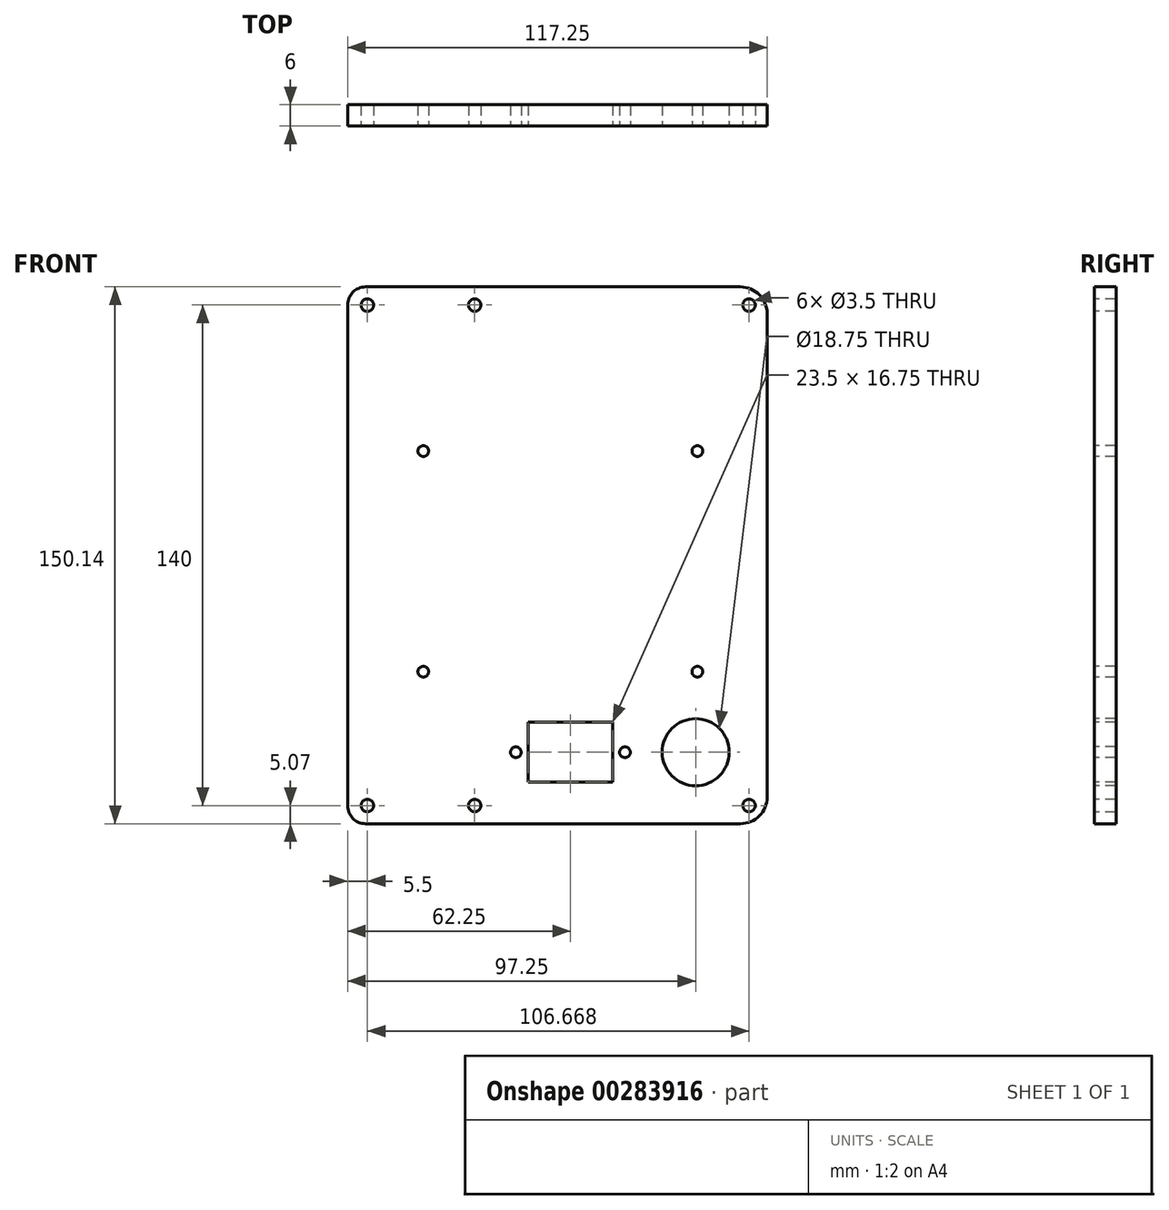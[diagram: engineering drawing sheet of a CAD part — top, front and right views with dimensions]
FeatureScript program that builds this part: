
annotation { "Feature Type Name" : "Feature", "Feature Type Description" : "" }
export const myFeature = defineFeature(function(context is Context, id is Id, definition is map)
    precondition{}
    {
        {
            var Q0;
            Q0=qCreatedBy(makeId("Front.planeOp"),FACE);
            var sketch = newSketch(context, id + "F0", { "sketchPlane" : qUnion([Q0])});
            skLineSegment(sketch, "E0.bottom", {"start": v(20.5, 75.07) * mm, "end": v(-20.5, 75.07) * mm});
            skLineSegment(sketch, "E0.top", {"start": v(20.5, -75.07) * mm, "end": v(-20.5, -75.07) * mm});
            skLineSegment(sketch, "E0.left", {"start": v(20.5, 75.07) * mm, "end": v(20.5, -75.07) * mm});
            skLineSegment(sketch, "E0.right", {"start": v(-20.5, 75.07) * mm, "end": v(-20.5, -75.07) * mm});
            skPoint(sketch, "E0.middle", {"position": v(0, 0) * mm});
            skSolve(sketch);
        }
        {
            var Q0;
            Q0 = qSketchRegion(id + "F0", true);
            extrude(context, id + "F1", {"entities" : qUnion([Q0]), "depth" : 6 * mm});
        }
        {
            var Q0;
            Q0=makeQuery(id+"F1.opExtrude","CAP_FACE",FACE,{"disambiguationData":[OSD([sQuery(id+"F0.wireOp",EDGE,"E0.bottom"),sQuery(id+"F0.wireOp",EDGE,"E0.top"),sQuery(id+"F0.wireOp",EDGE,"E0.left"),sQuery(id+"F0.wireOp",EDGE,"E0.right")])],"isStart":false});
            var sketch = newSketch(context, id + "F2", { "sketchPlane" : qUnion([Q0])});
            skLineSegment(sketch, "E1", {"start": v(0, 75.07) * mm, "end": v(0, 0) * mm, "construction": true});
            skLineSegment(sketch, "E2", {"start": v(0, 0) * mm, "end": v(-20.5, 0) * mm, "construction": true});
            skCircle(sketch, "E3", {"center": v(-15, 70) * mm, "radius": 1.75 * mm});
            skCircle(sketch, "E4.MirrorC", {"center": v(15, 70) * mm, "radius": 1.75 * mm});
            skCircle(sketch, "E5.MirrorC", {"center": v(-15, -70) * mm, "radius": 1.75 * mm});
            skCircle(sketch, "E6.MirrorC", {"center": v(15, -70) * mm, "radius": 1.75 * mm});
            skSolve(sketch);
        }
        {
            var Q0;
            Q0 = qSketchRegion(id + "F2", true);
            extrude(context, id + "F3", {"entities" : qUnion([Q0]), "operationType" : NewBodyOperationType.REMOVE, "endBound" : BoundingType.THROUGH_ALL, "oppositeDirection" : true, "depth" : 25 * mm});
        }
        {
            var Q0;
            Q0=makeQuery(id+"F1.opExtrude","CAP_FACE",FACE,{"disambiguationData":[OSD([sQuery(id+"F0.wireOp",EDGE,"E0.bottom"),sQuery(id+"F0.wireOp",EDGE,"E0.top"),sQuery(id+"F0.wireOp",EDGE,"E0.left"),sQuery(id+"F0.wireOp",EDGE,"E0.right")])],"isStart":false});
            var sketch = newSketch(context, id + "F4", { "sketchPlane" : qUnion([Q0])});
            skLineSegment(sketch, "E7.bottom", {"start": v(20.5, 75.07) * mm, "end": v(96.75, 75.07) * mm});
            skLineSegment(sketch, "E7.top", {"start": v(20.5, -75.07) * mm, "end": v(96.75, -75.07) * mm});
            skLineSegment(sketch, "E7.left", {"start": v(20.5, 75.07) * mm, "end": v(20.5, -75.07) * mm});
            skLineSegment(sketch, "E7.right", {"start": v(96.75, 75.07) * mm, "end": v(96.75, -75.07) * mm});
            skSolve(sketch);
        }
        {
            var Q0;
            Q0 = qSketchRegion(id + "F4", true);
            var Q1;
            Q1=makeQuery(id+"F1.opExtrude","CAP_FACE",FACE,{"disambiguationData":[OSD([sQuery(id+"F0.wireOp",EDGE,"E0.bottom"),sQuery(id+"F0.wireOp",EDGE,"E0.top"),sQuery(id+"F0.wireOp",EDGE,"E0.left"),sQuery(id+"F0.wireOp",EDGE,"E0.right")])],"isStart":true});
            extrude(context, id + "F5", {"entities" : qUnion([Q0]), "operationType" : NewBodyOperationType.ADD, "endBound" : BoundingType.UP_TO_SURFACE, "oppositeDirection" : true, "endBoundEntityFace" : qUnion([Q1]), "depth" : 25 * mm});
        }
        {
            var Q0;
            Q0=makeQuery(id+"F1.opExtrude","SWEPT_EDGE",EDGE,{"disambiguationData":[OSD([sQuery(id+"F0.wireOp",EDGE,"E0.bottom"),sQuery(id+"F0.wireOp",EDGE,"E0.right")])]});
            var Q1;
            Q1=makeQuery(id+"F1.opExtrude","SWEPT_EDGE",EDGE,{"disambiguationData":[OSD([sQuery(id+"F0.wireOp",EDGE,"E0.top"),sQuery(id+"F0.wireOp",EDGE,"E0.right")])]});
            fillet(context, id + "F6", {"entities" : qUnion([Q0, Q1]), "radius" : 5 * mm, "tangentPropagation" : true, "allowEdgeOverflow" : false});
        }
        {
            var Q0;
            Q0=makeQuery(id+"F5.opExtrude","SWEPT_EDGE",EDGE,{"disambiguationData":[OSD([sQuery(id+"F4.wireOp",EDGE,"E7.bottom"),sQuery(id+"F4.wireOp",EDGE,"E7.right")])]});
            var Q1;
            Q1=makeQuery(id+"F5.opExtrude","SWEPT_EDGE",EDGE,{"disambiguationData":[OSD([sQuery(id+"F4.wireOp",EDGE,"E7.top"),sQuery(id+"F4.wireOp",EDGE,"E7.right")])]});
            fillet(context, id + "F7", {"entities" : qUnion([Q0, Q1]), "radius" : 7.5 * mm, "tangentPropagation" : true, "allowEdgeOverflow" : false});
        }
        {
            var Q0;
            Q0=makeQuery(id+"F5.boolean.opBoolean","MERGE",FACE,{"derivedFrom":[makeQuery(id+"F1.opExtrude","CAP_FACE",FACE,{"disambiguationData":[OSD([sQuery(id+"F0.wireOp",EDGE,"E0.bottom"),sQuery(id+"F0.wireOp",EDGE,"E0.top"),sQuery(id+"F0.wireOp",EDGE,"E0.left"),sQuery(id+"F0.wireOp",EDGE,"E0.right")])],"isStart":false}),makeQuery(id+"F5.opExtrude","CAP_FACE",FACE,{"disambiguationData":[OSD([sQuery(id+"F4.wireOp",EDGE,"E7.bottom"),sQuery(id+"F4.wireOp",EDGE,"E7.top"),sQuery(id+"F4.wireOp",EDGE,"E7.left"),sQuery(id+"F4.wireOp",EDGE,"E7.right")])],"isStart":true})]});
            var sketch = newSketch(context, id + "F8", { "sketchPlane" : qUnion([Q0])});
            skLineSegment(sketch, "E8", {"start": v(15, 70) * mm, "end": v(91.67, 70) * mm, "construction": true});
            skCircle(sketch, "E9", {"center": v(91.67, 70) * mm, "radius": 1.75 * mm});
            skLineSegment(sketch, "E10", {"start": v(15, -70) * mm, "end": v(91.67, -70) * mm, "construction": true});
            skCircle(sketch, "E11", {"center": v(91.67, -70) * mm, "radius": 1.75 * mm});
            skSolve(sketch);
        }
        {
            var Q0;
            Q0 = qSketchRegion(id + "F8", true);
            extrude(context, id + "F9", {"entities" : qUnion([Q0]), "operationType" : NewBodyOperationType.REMOVE, "endBound" : BoundingType.THROUGH_ALL, "oppositeDirection" : true, "depth" : 25 * mm});
        }
        {
            var Q0;
            Q0=makeQuery(id+"F5.boolean.opBoolean","MERGE",FACE,{"derivedFrom":[makeQuery(id+"F1.opExtrude","CAP_FACE",FACE,{"disambiguationData":[OSD([sQuery(id+"F0.wireOp",EDGE,"E0.bottom"),sQuery(id+"F0.wireOp",EDGE,"E0.top"),sQuery(id+"F0.wireOp",EDGE,"E0.left"),sQuery(id+"F0.wireOp",EDGE,"E0.right")])],"isStart":false}),makeQuery(id+"F5.opExtrude","CAP_FACE",FACE,{"disambiguationData":[OSD([sQuery(id+"F4.wireOp",EDGE,"E7.bottom"),sQuery(id+"F4.wireOp",EDGE,"E7.top"),sQuery(id+"F4.wireOp",EDGE,"E7.left"),sQuery(id+"F4.wireOp",EDGE,"E7.right")])],"isStart":true})]});
            var sketch = newSketch(context, id + "F10", { "sketchPlane" : qUnion([Q0])});
            skCircle(sketch, "E12", {"center": v(76.75, -55.07) * mm, "radius": 9.38 * mm});
            skLineSegment(sketch, "E13.bottom", {"start": v(53.5, -46.7) * mm, "end": v(30, -46.7) * mm});
            skLineSegment(sketch, "E13.top", {"start": v(53.5, -63.45) * mm, "end": v(30, -63.45) * mm});
            skLineSegment(sketch, "E13.left", {"start": v(53.5, -46.7) * mm, "end": v(53.5, -63.45) * mm});
            skLineSegment(sketch, "E13.right", {"start": v(30, -46.7) * mm, "end": v(30, -63.45) * mm});
            skPoint(sketch, "E13.middle", {"position": v(41.75, -55.07) * mm});
            skLineSegment(sketch, "E14", {"start": v(76.75, -55.07) * mm, "end": v(41.75, -55.07) * mm, "construction": true});
            skCircle(sketch, "E15", {"center": v(57, -55.07) * mm, "radius": 1.5 * mm});
            skLineSegment(sketch, "E16", {"start": v(41.75, -46.7) * mm, "end": v(41.75, -55.07) * mm, "construction": true});
            skCircle(sketch, "E17.MirrorC", {"center": v(26.5, -55.07) * mm, "radius": 1.5 * mm});
            skSolve(sketch);
        }
        {
            var Q0;
            Q0 = qSketchRegion(id + "F10", true);
            extrude(context, id + "F11", {"entities" : qUnion([Q0]), "operationType" : NewBodyOperationType.REMOVE, "endBound" : BoundingType.THROUGH_ALL, "oppositeDirection" : true, "depth" : 25 * mm});
        }
        {
            var Q0;
            Q0=makeQuery(id+"F5.boolean.opBoolean","MERGE",FACE,{"derivedFrom":[makeQuery(id+"F1.opExtrude","CAP_FACE",FACE,{"disambiguationData":[OSD([sQuery(id+"F0.wireOp",EDGE,"E0.bottom"),sQuery(id+"F0.wireOp",EDGE,"E0.top"),sQuery(id+"F0.wireOp",EDGE,"E0.left"),sQuery(id+"F0.wireOp",EDGE,"E0.right")])],"isStart":false}),makeQuery(id+"F5.opExtrude","CAP_FACE",FACE,{"disambiguationData":[OSD([sQuery(id+"F4.wireOp",EDGE,"E7.bottom"),sQuery(id+"F4.wireOp",EDGE,"E7.top"),sQuery(id+"F4.wireOp",EDGE,"E7.left"),sQuery(id+"F4.wireOp",EDGE,"E7.right")])],"isStart":true})]});
            var sketch = newSketch(context, id + "F12", { "sketchPlane" : qUnion([Q0])});
            skLineSegment(sketch, "E18.bottom", {"start": v(-13.38, 33.3) * mm, "end": v(87.13, 33.3) * mm, "construction": true});
            skLineSegment(sketch, "E18.top", {"start": v(-13.37, -36.7) * mm, "end": v(87.13, -36.7) * mm, "construction": true});
            skLineSegment(sketch, "E18.left", {"start": v(-13.38, 33.3) * mm, "end": v(-13.38, -36.7) * mm, "construction": true});
            skLineSegment(sketch, "E18.right", {"start": v(87.13, 33.3) * mm, "end": v(87.13, -36.7) * mm, "construction": true});
            skLineSegment(sketch, "E19", {"start": v(36.88, 75.07) * mm, "end": v(36.88, 33.3) * mm, "construction": true});
            skLineSegment(sketch, "E20", {"start": v(-13.37, -1.7) * mm, "end": v(87.13, -1.7) * mm, "construction": true});
            skCircle(sketch, "E21", {"center": v(0.63, -32.55) * mm, "radius": 1.5 * mm});
            skCircle(sketch, "E22", {"center": v(77.23, -32.55) * mm, "radius": 1.5 * mm});
            skCircle(sketch, "E23.MirrorC", {"center": v(0.63, 29.16) * mm, "radius": 1.5 * mm});
            skCircle(sketch, "E24.MirrorC", {"center": v(77.23, 29.16) * mm, "radius": 1.5 * mm});
            skSolve(sketch);
        }
        {
            var Q0;
            Q0 = qSketchRegion(id + "F12", true);
            extrude(context, id + "F13", {"entities" : qUnion([Q0]), "operationType" : NewBodyOperationType.REMOVE, "endBound" : BoundingType.THROUGH_ALL, "oppositeDirection" : true, "depth" : 25 * mm});
        }
    });
